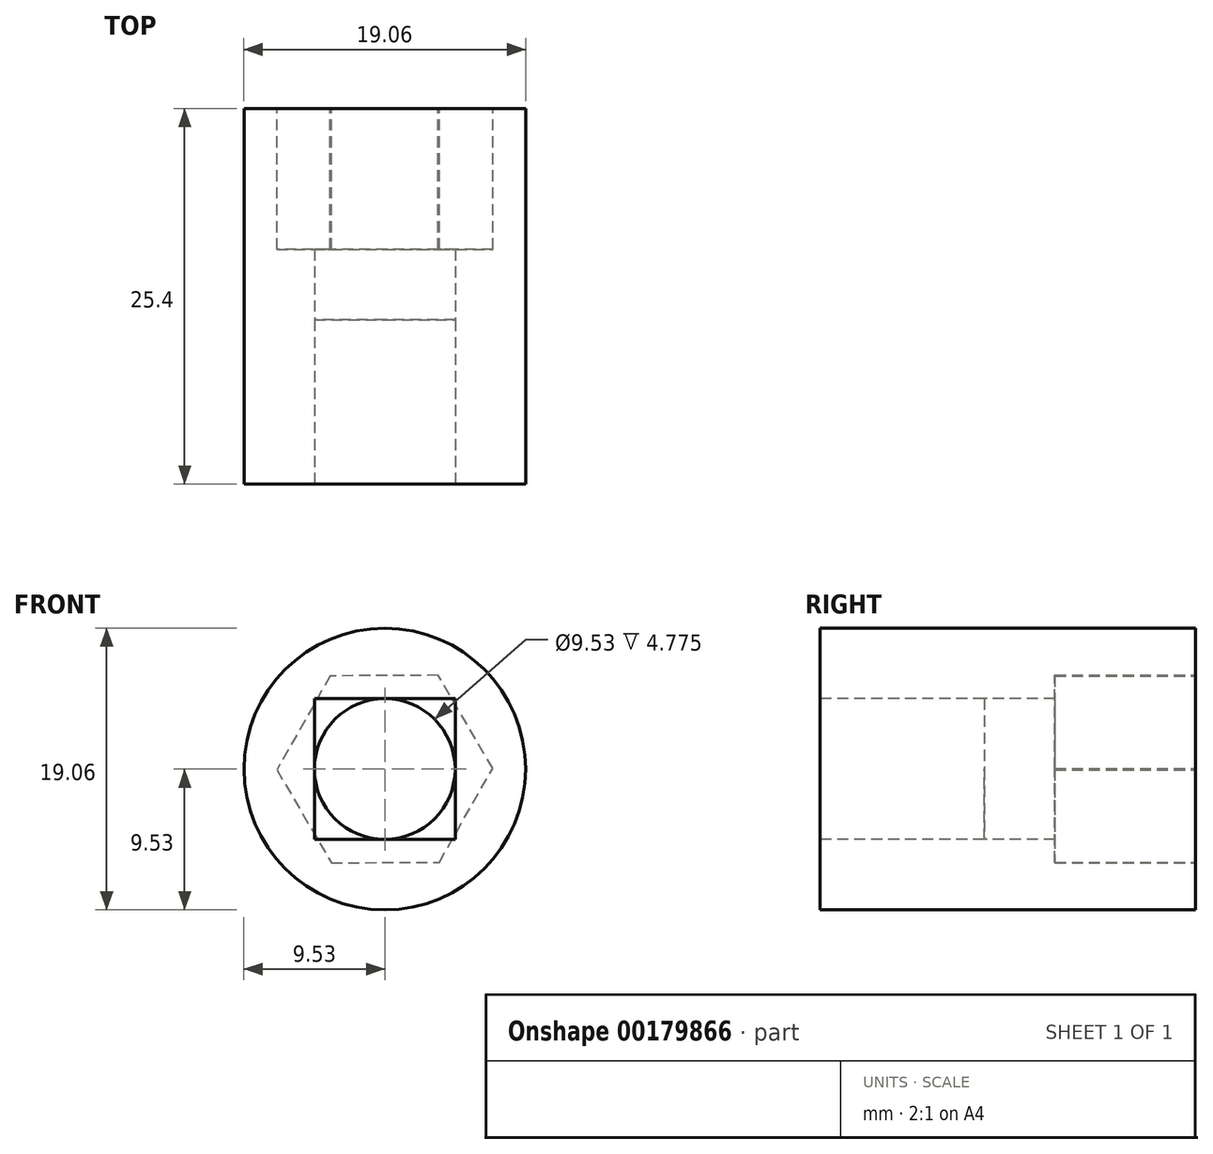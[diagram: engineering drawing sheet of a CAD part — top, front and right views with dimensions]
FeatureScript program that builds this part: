
annotation { "Feature Type Name" : "Feature", "Feature Type Description" : "" }
export const myFeature = defineFeature(function(context is Context, id is Id, definition is map)
    precondition{}
    {
        {
            var Q0;
            Q0=qCreatedBy(makeId("Front.planeOp"),FACE);
            var sketch = newSketch(context, id + "F0", { "sketchPlane" : qUnion([Q0])});
            skCircle(sketch, "E0", {"center": v(0, 0) * mm, "radius": 9.53 * mm});
            skSolve(sketch);
        }
        {
            var Q0;
            Q0 = qSketchRegion(id + "F0", true);
            extrude(context, id + "F1", {"entities" : qUnion([Q0]), "depth" : 25.4 * mm});
        }
        {
            var Q0;
            Q0=makeQuery(id+"F1.opExtrude","CAP_FACE",FACE,{"disambiguationData":[OSD([sQuery(id+"F0.wireOp",EDGE,"E0")])],"isStart":false});
            var sketch = newSketch(context, id + "F2", { "sketchPlane" : qUnion([Q0])});
            skLineSegment(sketch, "E1.bottom", {"start": v(-4.76, 4.76) * mm, "end": v(4.76, 4.76) * mm});
            skLineSegment(sketch, "E1.top", {"start": v(-4.76, -4.76) * mm, "end": v(4.76, -4.76) * mm});
            skLineSegment(sketch, "E1.left", {"start": v(-4.76, 4.76) * mm, "end": v(-4.76, -4.76) * mm});
            skLineSegment(sketch, "E1.right", {"start": v(4.76, 4.76) * mm, "end": v(4.76, -4.76) * mm});
            skPoint(sketch, "E1.middle", {"position": v(0, 0) * mm});
            skCircle(sketch, "E2", {"center": v(0, 0) * mm, "radius": 4.76 * mm});
            skSolve(sketch);
        }
        {
            var Q0;
            {var subQ0=sQuery(id+"F2.wireOp",EDGE,"E2");var subQ1=makeQuery(id+"F2.imprint","INTERSECT",VERTEX,{"derivedFrom":[sQuery(id+"F2.wireOp",EDGE,"E1.bottom"),subQ0]});Q0=makeQuery(id+"F2.imprint","IMPRINT",FACE,{"disambiguationData":[TD([[makeQuery(id+"F2.imprint","IMPRINT",EDGE,{"disambiguationData":[TD([[subQ1,1.0]])],"derivedFrom":subQ0}),1.0]])]});}
            extrude(context, id + "F3", {"entities" : qUnion([Q0]), "operationType" : NewBodyOperationType.REMOVE, "oppositeDirection" : true, "depth" : 25.4 * mm, "hasSecondDirection" : true, "secondDirectionBound" : SecondDirectionBoundingType.THROUGH_ALL, "secondDirectionOppositeDirection" : false, "secondDirectionDepth" : 25.4 * mm});
        }
        {
            var Q0;
            Q0 = qSketchRegion(id + "F2", true);
            extrude(context, id + "F4", {"entities" : qUnion([Q0]), "operationType" : NewBodyOperationType.REMOVE, "oppositeDirection" : true, "depth" : 11.1 * mm});
        }
        {
            var Q0;
            Q0=makeQuery(id+"F1.opExtrude","CAP_FACE",FACE,{"disambiguationData":[OSD([sQuery(id+"F0.wireOp",EDGE,"E0")])],"isStart":true});
            var sketch = newSketch(context, id + "F5", { "sketchPlane" : qUnion([Q0])});
            skSolve(sketch);
        }
        {
            var Q0;
            Q0=makeQuery(id+"F5.imprint","IMPRINT",FACE,{"disambiguationData":[TD([[makeQuery(id+"F5.imprint","IMPRINT",EDGE,{"derivedFrom":makeQuery(id+"F1.opExtrude","CAP_EDGE",EDGE,{"disambiguationData":[OSD([sQuery(id+"F0.wireOp",EDGE,"E0")])],"isStart":true})}),-1.0]])]});
            var sketch = newSketch(context, id + "F6", { "sketchPlane" : qUnion([Q0])});
            skCircle(sketch, "E3.cCircle", {"center": v(0, 0) * mm, "radius": 6.32 * mm, "construction": true});
            skLineSegment(sketch, "E3.0", {"start": v(7.3, -0.04) * mm, "end": v(3.62, -6.34) * mm});
            skLineSegment(sketch, "E3.1", {"start": v(3.62, -6.34) * mm, "end": v(-3.69, -6.3) * mm});
            skLineSegment(sketch, "E3.2", {"start": v(-3.69, -6.3) * mm, "end": v(-7.3, 0.04) * mm});
            skLineSegment(sketch, "E3.3", {"start": v(-7.3, 0.04) * mm, "end": v(-3.62, 6.34) * mm});
            skLineSegment(sketch, "E3.4", {"start": v(-3.62, 6.34) * mm, "end": v(3.69, 6.3) * mm});
            skLineSegment(sketch, "E3.5", {"start": v(3.69, 6.3) * mm, "end": v(7.3, -0.04) * mm});
            skPoint(sketch, "E3.0.midPoint", {"position": v(5.46, -3.2) * mm});
            skSolve(sketch);
        }
        {
            var Q0;
            Q0 = qSketchRegion(id + "F6", true);
            extrude(context, id + "F7", {"entities" : qUnion([Q0]), "operationType" : NewBodyOperationType.REMOVE, "oppositeDirection" : true, "depth" : 9.52 * mm});
        }
    });
